# Revit family: X280 series automatic
name_source: partatom
category: Mechanical Equipment
revit_build: Autodesk Revit 2013 (Build: 20120221_2030(x64)
units: mm (PartAtom-declared; Revit-internal decimal feet)

## types (5) — shared parameters
Assembly Code = D2010900
Cooling = Oil Filled
Cord Length = 240"
Cord Type = UL listed, 5-wire (1 Ph)
Default Elevation = 0"
Description = Commercial Effluent Pumps
Discharge Diameter = 2" or 3" NPT Flange
Discharge Height = 6 5/16"
Discharge Radius = 1"
Hertz = 60
Impeller Type = Non-clogging vortex
Installation Type = Floor Mounted
Insulation = Class B
Length = 13 9/16"
Manufacturer = Zoeller
Masterformat Number = 33 36 16
Masterformat Title = Utility Septic Tank Effluent Pumps
Material = Cast Iron-Zoeller-Powder Coated Epoxy
Max. Operating Temp. = 104° F
Mechanical Seals = Carbon and ceramic with stainless steel parts
Model = X282
Motor Thermal Shutoff = Thermal Overload (1 Ph)
Motor Type = Submersible
Omniclass Table 23 Code = 23.60.30.21
Omniclass Table 23 Title = Pumps
Operation = Automatic
Overall Height = 25 3/16"
Phase = 1
Price = Prices may vary. Please consult Manufacturer Representative for most up-to-date price list.
Product Page URL = http://www.zoellerpumps.com
RPM = 1750
Shipping Weight = 135 lbs.
Solid Handling = 2" Spherical Solids
Square Ring & Gasket = Neoprene
Type = Permanent Split Capacitor
URL = http://www.zoellerpumps.com
Warranty Information = 36 Months (Limited)
Waste Connection = Yes
Width = 13 9/16"

## per-type parameters (varying)
| type | Amps | Apparent Load | Flow @ 5' | Impeller Diameter | Maximum Head | Motor | Voltage |
| X282-115V 1Ph | 10 A | 1185 VA | 127 GPM | 6 1/4" | 312" | 1/2 HP | 115 V |
| X282-230V 1Ph | 5 A | 1150 VA | 127 GPM | 6 1/4" | 312" | 1/2 HP | 230 V |
| X282-200V 1Ph | 6 A | 1220 VA | 127 GPM | 6 1/4" | 312" | 1/2 HP | 200 V |
| X284-230V 1Ph | 9 A | 2047 VA | 179 GPM | 6 1/2" | 420" | 1 HP | 230 V |
| X284-200V 1Ph | 9 A | 1860 VA | 179 GPM | 6 1/2" | 420" | 1 HP | 200 V |

## geometry (parser evidence)
native form markers: Blend x12, Sweep x3
no freeform markers — native parametric forms only
